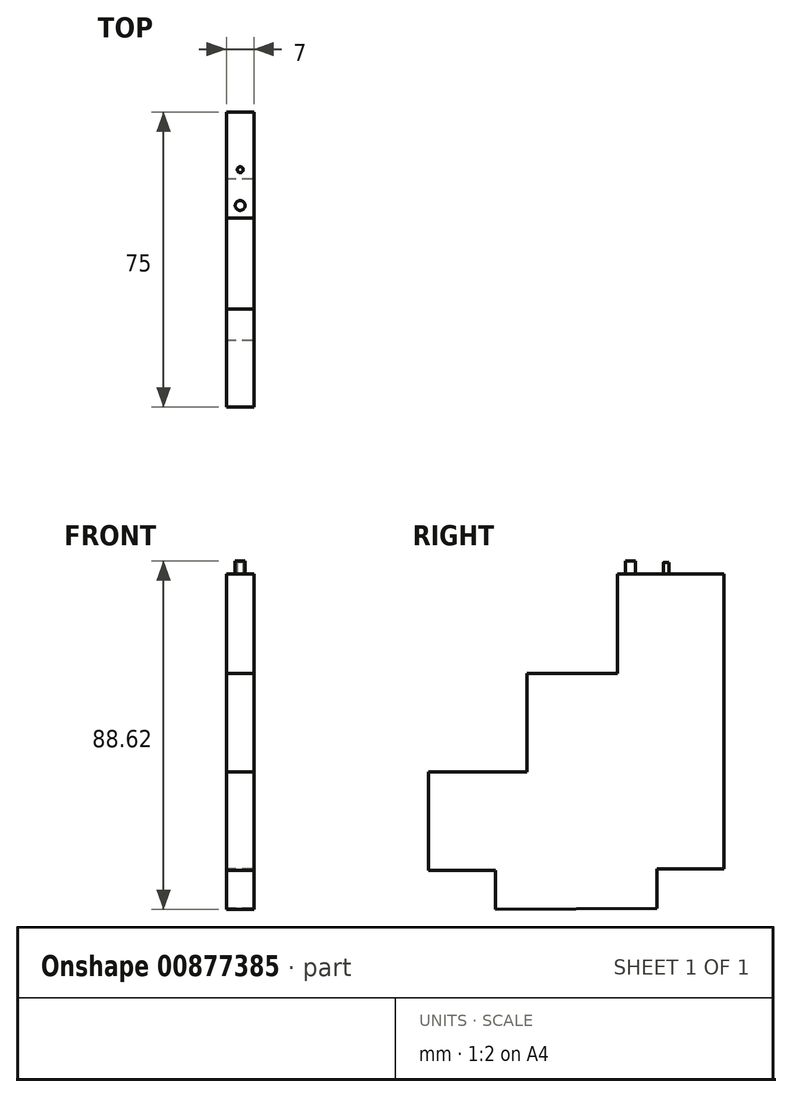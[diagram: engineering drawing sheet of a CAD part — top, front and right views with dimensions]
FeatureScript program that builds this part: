
annotation { "Feature Type Name" : "Feature", "Feature Type Description" : "" }
export const myFeature = defineFeature(function(context is Context, id is Id, definition is map)
    precondition{}
    {
        {
            var Q0;
            Q0=qCreatedBy(makeId("Right.planeOp"),FACE);
            var sketch = newSketch(context, id + "F0", { "sketchPlane" : qUnion([Q0])});
            skLineSegment(sketch, "E0", {"start": v(-25.67, -12.62) * mm, "end": v(-25.67, 12.38) * mm});
            skLineSegment(sketch, "E1", {"start": v(-25.67, 12.38) * mm, "end": v(-0.67, 12.38) * mm});
            skLineSegment(sketch, "E2", {"start": v(-0.67, 12.38) * mm, "end": v(-0.67, 37.38) * mm});
            skLineSegment(sketch, "E3", {"start": v(-0.67, 37.38) * mm, "end": v(22.33, 37.38) * mm});
            skLineSegment(sketch, "E4", {"start": v(22.33, 37.38) * mm, "end": v(22.33, 62.67) * mm});
            skLineSegment(sketch, "E5", {"start": v(49.33, 62.67) * mm, "end": v(49.33, -12.33) * mm});
            skLineSegment(sketch, "E6", {"start": v(-25.67, -12.62) * mm, "end": v(-8.67, -12.62) * mm});
            skLineSegment(sketch, "E7", {"start": v(-8.67, -12.62) * mm, "end": v(-8.67, -22.62) * mm});
            skLineSegment(sketch, "E8", {"start": v(49.33, -12.33) * mm, "end": v(32.33, -12.33) * mm});
            skLineSegment(sketch, "E9", {"start": v(32.33, -12.33) * mm, "end": v(32.33, -22.33) * mm});
            skLineSegment(sketch, "E10", {"start": v(-8.67, -22.62) * mm, "end": v(32.33, -22.33) * mm});
            skLineSegment(sketch, "E11", {"start": v(22.33, 62.67) * mm, "end": v(26.76, 62.67) * mm});
            skLineSegment(sketch, "E12", {"start": v(26.76, 62.67) * mm, "end": v(49.33, 62.67) * mm});
            skSolve(sketch);
        }
        {
            var Q0;
            Q0 = qSketchRegion(id + "F0", true);
            var Q1;
            Q1 = qSketchRegion(id + "F2", true);
            extrude(context, id + "F1", {"entities" : qUnion([Q0, Q1]), "depth" : 7 * mm, "offsetDistance" : 25 * mm});
        }
        {
            var Q0;
            Q0=qCreatedBy(makeId("Top.planeOp"),FACE);
            var sketch = newSketch(context, id + "F2", { "sketchPlane" : qUnion([Q0])});
            skPoint(sketch, "E13", {"position": v(0, 25.59) * mm});
            skPoint(sketch, "E14", {"position": v(7, 25.59) * mm});
            skLineSegment(sketch, "E15", {"start": v(0, 25.59) * mm, "end": v(7, 25.59) * mm, "construction": true});
            skPoint(sketch, "E16", {"position": v(0, 26.84) * mm});
            skLineSegment(sketch, "E17", {"start": v(0, 26.84) * mm, "end": v(0, 24.34) * mm, "construction": true});
            skLineSegment(sketch, "E18", {"start": v(0, 24.34) * mm, "end": v(0, 25.59) * mm, "construction": true});
            skPoint(sketch, "E19", {"position": v(3.5, 25.59) * mm});
            skCircle(sketch, "E20", {"center": v(3.5, 25.59) * mm, "radius": 1.25 * mm});
            skPoint(sketch, "E21", {"position": v(7, 26.84) * mm});
            skLineSegment(sketch, "E22", {"start": v(0, 26.84) * mm, "end": v(7, 26.84) * mm, "construction": true});
            skPoint(sketch, "E23", {"position": v(3.5, 26.84) * mm});
            skPoint(sketch, "E24", {"position": v(3.5, 33.94) * mm});
            skLineSegment(sketch, "E25", {"start": v(3.5, 33.94) * mm, "end": v(3.5, 26.84) * mm, "construction": true});
            skPoint(sketch, "E26", {"position": v(0, 33.94) * mm});
            skPoint(sketch, "E27", {"position": v(7, 33.94) * mm});
            skLineSegment(sketch, "E28", {"start": v(0, 33.94) * mm, "end": v(3.5, 33.94) * mm, "construction": true});
            skLineSegment(sketch, "E29", {"start": v(3.5, 33.94) * mm, "end": v(7, 33.94) * mm, "construction": true});
            skLineSegment(sketch, "E30", {"start": v(3.5, 33.94) * mm, "end": v(3.5, 34.69) * mm, "construction": true});
            skPoint(sketch, "E31", {"position": v(3.5, 34.69) * mm});
            skPoint(sketch, "E32", {"position": v(0, 34.69) * mm});
            skLineSegment(sketch, "E33", {"start": v(0, 34.69) * mm, "end": v(3.5, 34.69) * mm, "construction": true});
            skCircle(sketch, "E34", {"center": v(3.5, 34.69) * mm, "radius": 0.75 * mm});
            skSolve(sketch);
        }
        {
            var Q0;
            Q0 = qSketchRegion(id + "F2", true);
            extrude(context, id + "F3", {"entities" : qUnion([Q0]), "operationType" : NewBodyOperationType.ADD, "depth" : 25 * mm, "offsetDistance" : 25 * mm});
        }
        {
            var Q0;
            Q0 = qSketchRegion(id + "F2", true);
            extrude(context, id + "F4", {"entities" : qUnion([Q0]), "operationType" : NewBodyOperationType.ADD, "depth" : 25 * mm, "offsetDistance" : 25 * mm});
        }
        {
            var Q0;
            Q0=makeQuery(id+"F2.imprint","IMPRINT",FACE,{"disambiguationData":[TD([[makeQuery(id+"F2.imprint","IMPRINT",EDGE,{"derivedFrom":sQuery(id+"F2.wireOp",EDGE,"E20")}),1.0]])]});
            extrude(context, id + "F5", {"entities" : qUnion([Q0]), "operationType" : NewBodyOperationType.ADD, "depth" : 66 * mm, "offsetDistance" : 25 * mm});
        }
        {
            var Q0;
            Q0=makeQuery(id+"F2.imprint","IMPRINT",FACE,{"disambiguationData":[TD([[makeQuery(id+"F2.imprint","IMPRINT",EDGE,{"derivedFrom":sQuery(id+"F2.wireOp",EDGE,"E34")}),1.0]])]});
            extrude(context, id + "F6", {"entities" : qUnion([Q0]), "operationType" : NewBodyOperationType.ADD, "depth" : 65.5 * mm, "offsetDistance" : 25 * mm});
        }
    });
